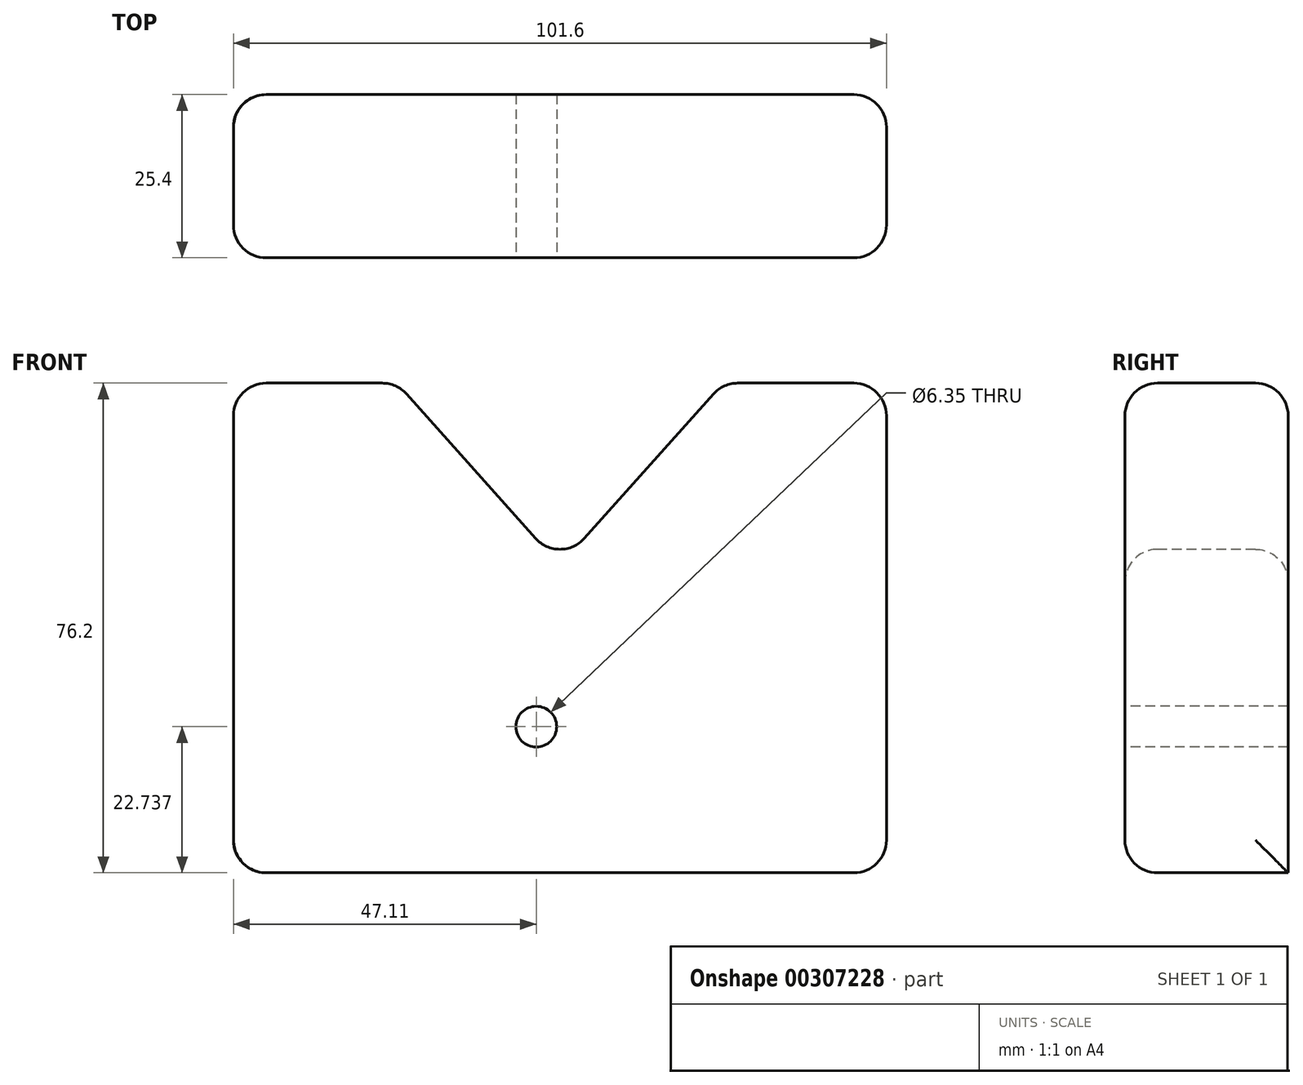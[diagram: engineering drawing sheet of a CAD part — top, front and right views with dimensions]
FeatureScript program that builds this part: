
annotation { "Feature Type Name" : "Feature", "Feature Type Description" : "" }
export const myFeature = defineFeature(function(context is Context, id is Id, definition is map)
    precondition{}
    {
        {
            var Q0;
            Q0=qCreatedBy(makeId("Front.planeOp"),FACE);
            var sketch = newSketch(context, id + "F0", { "sketchPlane" : qUnion([Q0])});
            skLineSegment(sketch, "E0", {"start": v(-47.1, -67.36) * mm, "end": v(54.5, -67.36) * mm});
            skLineSegment(sketch, "E1", {"start": v(54.5, -67.36) * mm, "end": v(54.5, 8.84) * mm});
            skLineSegment(sketch, "E2", {"start": v(54.5, 8.84) * mm, "end": v(29.1, 8.84) * mm});
            skLineSegment(sketch, "E3", {"start": v(29.1, 8.84) * mm, "end": v(3.7, -19.56) * mm});
            skLineSegment(sketch, "E4", {"start": v(3.7, -19.56) * mm, "end": v(-21.7, 8.84) * mm});
            skLineSegment(sketch, "E5", {"start": v(-21.7, 8.84) * mm, "end": v(-47.1, 8.84) * mm});
            skLineSegment(sketch, "E6", {"start": v(-47.1, 8.84) * mm, "end": v(-47.1, -67.36) * mm});
            skSolve(sketch);
        }
        {
            var Q0;
            Q0=makeQuery(id+"F0.imprint","IMPRINT",FACE,{"disambiguationData":[TD([[makeQuery(id+"F0.imprint","IMPRINT",EDGE,{"derivedFrom":sQuery(id+"F0.wireOp",EDGE,"E0")}),1.0]])]});
            extrude(context, id + "F1", {"entities" : qUnion([Q0]), "depth" : 25.4 * mm});
        }
        {
            var Q0;
            Q0=makeQuery(id+"F1.opExtrude","SWEPT_FACE",FACE,{"disambiguationData":[OSD([sQuery(id+"F0.wireOp",EDGE,"E5")])]});
            var Q1;
            Q1=makeQuery(id+"F1.opExtrude","SWEPT_FACE",FACE,{"disambiguationData":[OSD([sQuery(id+"F0.wireOp",EDGE,"E2")])]});
            var Q2;
            Q2=makeQuery(id+"F1.opExtrude","SWEPT_FACE",FACE,{"disambiguationData":[OSD([sQuery(id+"F0.wireOp",EDGE,"E1")])]});
            var Q3;
            Q3=makeQuery(id+"F1.opExtrude","CAP_FACE",FACE,{"disambiguationData":[OSD([sQuery(id+"F0.wireOp",EDGE,"E0"),sQuery(id+"F0.wireOp",EDGE,"E1"),sQuery(id+"F0.wireOp",EDGE,"E2"),sQuery(id+"F0.wireOp",EDGE,"E3"),sQuery(id+"F0.wireOp",EDGE,"E4"),sQuery(id+"F0.wireOp",EDGE,"E5"),sQuery(id+"F0.wireOp",EDGE,"E6")])],"isStart":false});
            var Q4;
            Q4=makeQuery(id+"F1.opExtrude","SWEPT_FACE",FACE,{"disambiguationData":[OSD([sQuery(id+"F0.wireOp",EDGE,"E4")])]});
            var Q5;
            Q5=makeQuery(id+"F1.opExtrude","SWEPT_FACE",FACE,{"disambiguationData":[OSD([sQuery(id+"F0.wireOp",EDGE,"E3")])]});
            var Q6;
            Q6=makeQuery(id+"F1.opExtrude","SWEPT_FACE",FACE,{"disambiguationData":[OSD([sQuery(id+"F0.wireOp",EDGE,"E6")])]});
            fillet(context, id + "F2", {"entities" : qUnion([Q0, Q1, Q2, Q3, Q4, Q5, Q6]), "radius" : 5.08 * mm, "tangentPropagation" : true, "allowEdgeOverflow" : false});
        }
        {
            var Q0;
            Q0=makeQuery(id+"F1.opExtrude","CAP_FACE",FACE,{"disambiguationData":[OSD([sQuery(id+"F0.wireOp",EDGE,"E0"),sQuery(id+"F0.wireOp",EDGE,"E1"),sQuery(id+"F0.wireOp",EDGE,"E2"),sQuery(id+"F0.wireOp",EDGE,"E3"),sQuery(id+"F0.wireOp",EDGE,"E4"),sQuery(id+"F0.wireOp",EDGE,"E5"),sQuery(id+"F0.wireOp",EDGE,"E6")])],"isStart":false});
            var sketch = newSketch(context, id + "F3", { "sketchPlane" : qUnion([Q0])});
            skCircle(sketch, "E7", {"center": v(0, -44.62) * mm, "radius": 19.48 * mm});
            skSolve(sketch);
        }
        {
            var Q0;
            Q0=sQuery(id+"F3.wireOp",VERTEX,"E7.center");
            var Q1;
            Q1=makeQuery(id+"F1.opExtrude","SWEPT_BODY",BODY,{"disambiguationData":[OSD([sQuery(id+"F0.wireOp",EDGE,"E0"),sQuery(id+"F0.wireOp",EDGE,"E1"),sQuery(id+"F0.wireOp",EDGE,"E2"),sQuery(id+"F0.wireOp",EDGE,"E3"),sQuery(id+"F0.wireOp",EDGE,"E4"),sQuery(id+"F0.wireOp",EDGE,"E5"),sQuery(id+"F0.wireOp",EDGE,"E6")])]});
            hole(context, id + "F4", {"style" : HoleStyle.SIMPLE, "endStyle" : HoleEndStyle.THROUGH, "holeDiameter" : 6.35 * mm, "tappedDepth" : 12.7 * mm, "tapClearance" : 3, "locations" : qUnion([Q0]), "scope" : qUnion([Q1])});
        }
    });
